# Revit family: Контейнерная площадка «Экология» Арт 19441
name_source: partatom
category: Антураж
revit_build: Autodesk Revit 2018 (Build: 20180423_1000(x64)
units: mm (PartAtom-declared; Revit-internal decimal feet)

## family parameters
Всегда вертикально = Да
Источник визуального образа = Геометрия семейства
На основе рабочей плоскости = Нет
Общий = Нет
При загрузке вырезать с полостями = Нет
Точка расчета площади = Нет

## types (3) — shared parameters
URL = https://hobbyka.ru
Артикул товара = Арт. 19441
Высота = 2268 мм
Группа модели = Контейнерные площадки для ТБО
Изготовитель = ООО «Хоббика»
Материал изделия = Сталь, дерево, профлист
Цвет каркаса = Сталь
Цвет крыши = Крыша
Цвет отделки = Дерево
Ширина = 2500 мм

## per-type parameters (varying)
| type | Версия 5,6 м | Версия 7,3 м | Версия 8,8 м | Длина | Изображение типоразмера | Описание |
| Версия 5,6 м | Да | Нет | Нет | 5600 мм | Контейнерная площадка «Экология» Арт 19441 5,6 м.jpg | Контейнерная площадка «Экология». Версия 5,6 м на 3 контейнера |
| Версия 7,3 м | Нет | Да | Нет | 7300 мм | Контейнерная площадка «Экология» Арт 19441.jpg | Контейнерная площадка «Экология». Версия 7,3 м на 4 контейнера |
| Версия 8,8 м | Нет | Нет | Да | 8800 мм | Контейнерная площадка «Экология» Арт 19441.jpg | Контейнерная площадка «Экология». Версия 8,8 м на 5 контейнеров |
